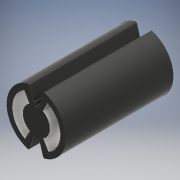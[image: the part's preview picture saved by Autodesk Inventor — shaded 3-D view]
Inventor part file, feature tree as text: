
AUTODESK INVENTOR PART (.ipt)
format: ipt  version: 2017 (Build 210142000, 142)  size: 158,208 bytes
history: native  units: mm
features: extrude x2, sketch x2
ambient origin geometry x8: Origin, YZ Plane, XZ Plane, XY Plane, X Axis, Y Axis, Z Axis, Center Point
bodies: Body1 (feature_tree)
feature tree (4):
  extrude  "Extrusion2"  Depth=42.0116mm
  extrude  "Extrusion3"  Depth=76.2mm
  sketch  "Sketch3"  dims[d18=18.9992mm d19=42.0116mm]
  sketch  "Sketch4"  dims[d20=2.4384mm d21=2.4384mm d22=76.2mm d23=0.0mm d25=2.4384mm d26=2.4384mm d27=76.2mm d28=0.0mm]
